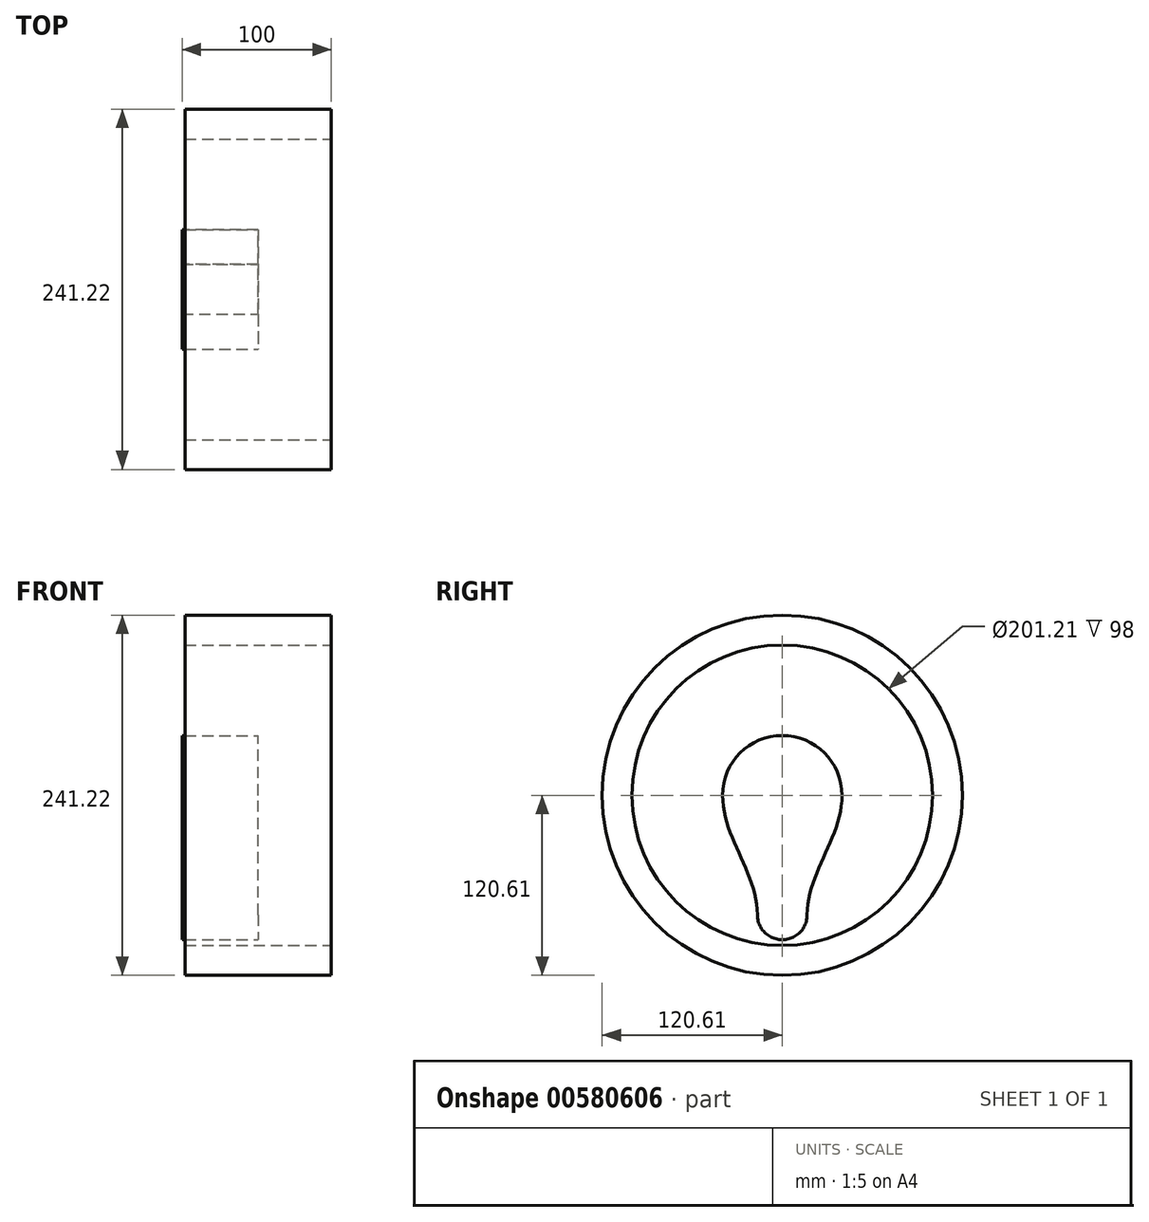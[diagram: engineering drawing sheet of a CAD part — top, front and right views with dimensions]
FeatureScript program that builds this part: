
annotation { "Feature Type Name" : "Feature", "Feature Type Description" : "" }
export const myFeature = defineFeature(function(context is Context, id is Id, definition is map)
    precondition{}
    {
        {
            var Q0;
            Q0=qCreatedBy(makeId("Right.planeOp"),FACE);
            var sketch = newSketch(context, id + "F0", { "sketchPlane" : qUnion([Q0])});
            skCircle(sketch, "E0", {"center": v(0, 0) * mm, "radius": 22.82 * mm});
            skSolve(sketch);
        }
        {
            var Q0;
            Q0 = qSketchRegion(id + "F0", true);
            extrude(context, id + "F1", {"entities" : qUnion([Q0]), "oppositeDirection" : true, "depth" : 34.54 * mm, "offsetDistance" : 25.4 * mm});
        }
        {
            var Q0;
            Q0=makeQuery(id+"F1.opExtrude","CAP_FACE",FACE,{"disambiguationData":[OSD([sQuery(id+"F0.wireOp",EDGE,"E0")])],"isStart":true});
            var sketch = newSketch(context, id + "F2", { "sketchPlane" : qUnion([Q0])});
            skArc(sketch, "E1", {"start": v(39.98, 0) * mm, "mid": v(0, 39.98) * mm, "end": v(-39.98, 0) * mm});
            skArc(sketch, "E2", {"start": v(-16.63, -80.05) * mm, "mid": v(0, -96.73) * mm, "end": v(16.63, -80.05) * mm});
            skFitSpline(sketch, "E3", {"points": [v(16.63, -80.05) * mm, v(39.98, 0) * mm], "startDerivative": vector(-0.24, 83.7) * mm, "endDerivative": vector(-0.07, 85.1) * mm});
            skLineSegment(sketch, "E4", {"start": v(0, -80.1) * mm, "end": v(0, 0) * mm, "construction": true});
            skFitSpline(sketch, "E5.MirrorCS", {"points": [v(-16.63, -80.05) * mm, v(-39.98, 0) * mm], "startDerivative": vector(0.24, 83.7) * mm, "endDerivative": vector(0.07, 85.1) * mm});
            skSolve(sketch);
        }
        {
            var Q0;
            Q0 = qSketchRegion(id + "F2", true);
            extrude(context, id + "F3", {"entities" : qUnion([Q0]), "operationType" : NewBodyOperationType.ADD, "oppositeDirection" : true, "depth" : 51 * mm, "offsetDistance" : 25 * mm});
        }
        {
            var Q0;
            Q0=makeQuery(id+"F3.boolean.opBoolean","MERGE",FACE,{"derivedFrom":[makeQuery(id+"F1.opExtrude","CAP_FACE",FACE,{"disambiguationData":[OSD([sQuery(id+"F0.wireOp",EDGE,"E0")])],"isStart":true}),makeQuery(id+"F3.opExtrude","CAP_FACE",FACE,{"disambiguationData":[OSD([sQuery(id+"F2.wireOp",EDGE,"E1"),sQuery(id+"F2.wireOp",EDGE,"E2"),sQuery(id+"F2.wireOp",EDGE,"E3"),sQuery(id+"F2.wireOp",EDGE,"E5.MirrorCS")])],"isStart":true})]});
            var sketch = newSketch(context, id + "F4", { "sketchPlane" : qUnion([Q0])});
            skCircle(sketch, "E6", {"center": v(0, 0) * mm, "radius": 100.6 * mm});
            skCircle(sketch, "E7.0", {"center": v(0, 0) * mm, "radius": 120.6 * mm});
            skSolve(sketch);
        }
        {
            var Q0;
            Q0 = qSketchRegion(id + "F4", true);
            extrude(context, id + "F5", {"entities" : qUnion([Q0]), "oppositeDirection" : true, "depth" : 98 * mm, "offsetDistance" : 25 * mm, "symmetric" : true});
        }
    });
